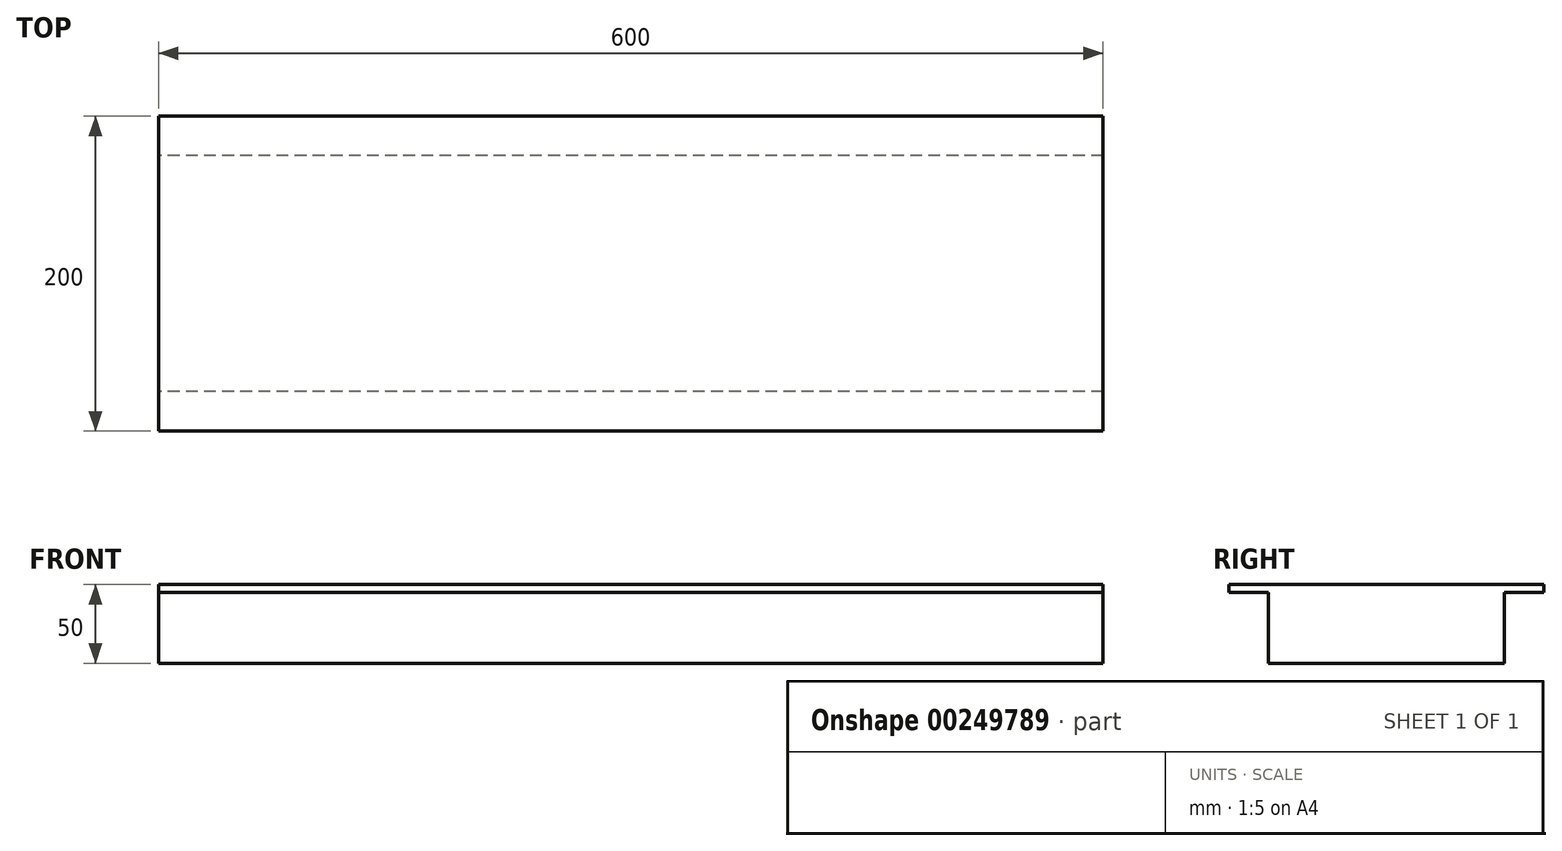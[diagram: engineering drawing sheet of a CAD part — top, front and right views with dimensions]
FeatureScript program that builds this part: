
annotation { "Feature Type Name" : "Feature", "Feature Type Description" : "" }
export const myFeature = defineFeature(function(context is Context, id is Id, definition is map)
    precondition{}
    {
        {
            var Q0;
            Q0=qCreatedBy(makeId("Top.planeOp"),FACE);
            var sketch = newSketch(context, id + "F0", { "sketchPlane" : qUnion([Q0])});
            skLineSegment(sketch, "E0.bottom", {"start": v(300, 100) * mm, "end": v(-300, 100) * mm});
            skLineSegment(sketch, "E0.top", {"start": v(300, -100) * mm, "end": v(-300, -100) * mm});
            skLineSegment(sketch, "E0.left", {"start": v(300, 100) * mm, "end": v(300, -100) * mm});
            skLineSegment(sketch, "E0.right", {"start": v(-300, 100) * mm, "end": v(-300, -100) * mm});
            skPoint(sketch, "E0.middle", {"position": v(0, 0) * mm});
            skSolve(sketch);
        }
        {
            var Q0;
            Q0=makeQuery(id+"F0.imprint","IMPRINT",FACE,{"disambiguationData":[TD([[makeQuery(id+"F0.imprint","IMPRINT",EDGE,{"derivedFrom":sQuery(id+"F0.wireOp",EDGE,"E0.bottom")}),1.0]])]});
            extrude(context, id + "F1", {"entities" : qUnion([Q0]), "depth" : 5 * mm});
        }
        {
            var Q0;
            Q0=makeQuery(id+"F1.opExtrude","CAP_FACE",FACE,{"disambiguationData":[OSD([sQuery(id+"F0.wireOp",EDGE,"E0.bottom"),sQuery(id+"F0.wireOp",EDGE,"E0.top"),sQuery(id+"F0.wireOp",EDGE,"E0.left"),sQuery(id+"F0.wireOp",EDGE,"E0.right")])],"isStart":true});
            var sketch = newSketch(context, id + "F2", { "sketchPlane" : qUnion([Q0])});
            skLineSegment(sketch, "E1.bottom", {"start": v(300, 75) * mm, "end": v(-300, 75) * mm});
            skLineSegment(sketch, "E1.top", {"start": v(300, -75) * mm, "end": v(-300, -75) * mm});
            skLineSegment(sketch, "E1.left", {"start": v(300, 75) * mm, "end": v(300, -75) * mm});
            skLineSegment(sketch, "E1.right", {"start": v(-300, 75) * mm, "end": v(-300, -75) * mm});
            skPoint(sketch, "E1.middle", {"position": v(0, 0) * mm});
            skSolve(sketch);
        }
        {
            var Q0;
            Q0=makeQuery(id+"F2.imprint","IMPRINT",FACE,{"disambiguationData":[TD([[makeQuery(id+"F2.imprint","IMPRINT",EDGE,{"derivedFrom":sQuery(id+"F2.wireOp",EDGE,"E1.bottom")}),1.0]])]});
            extrude(context, id + "F3", {"entities" : qUnion([Q0]), "operationType" : NewBodyOperationType.ADD, "depth" : 45 * mm});
        }
    });
